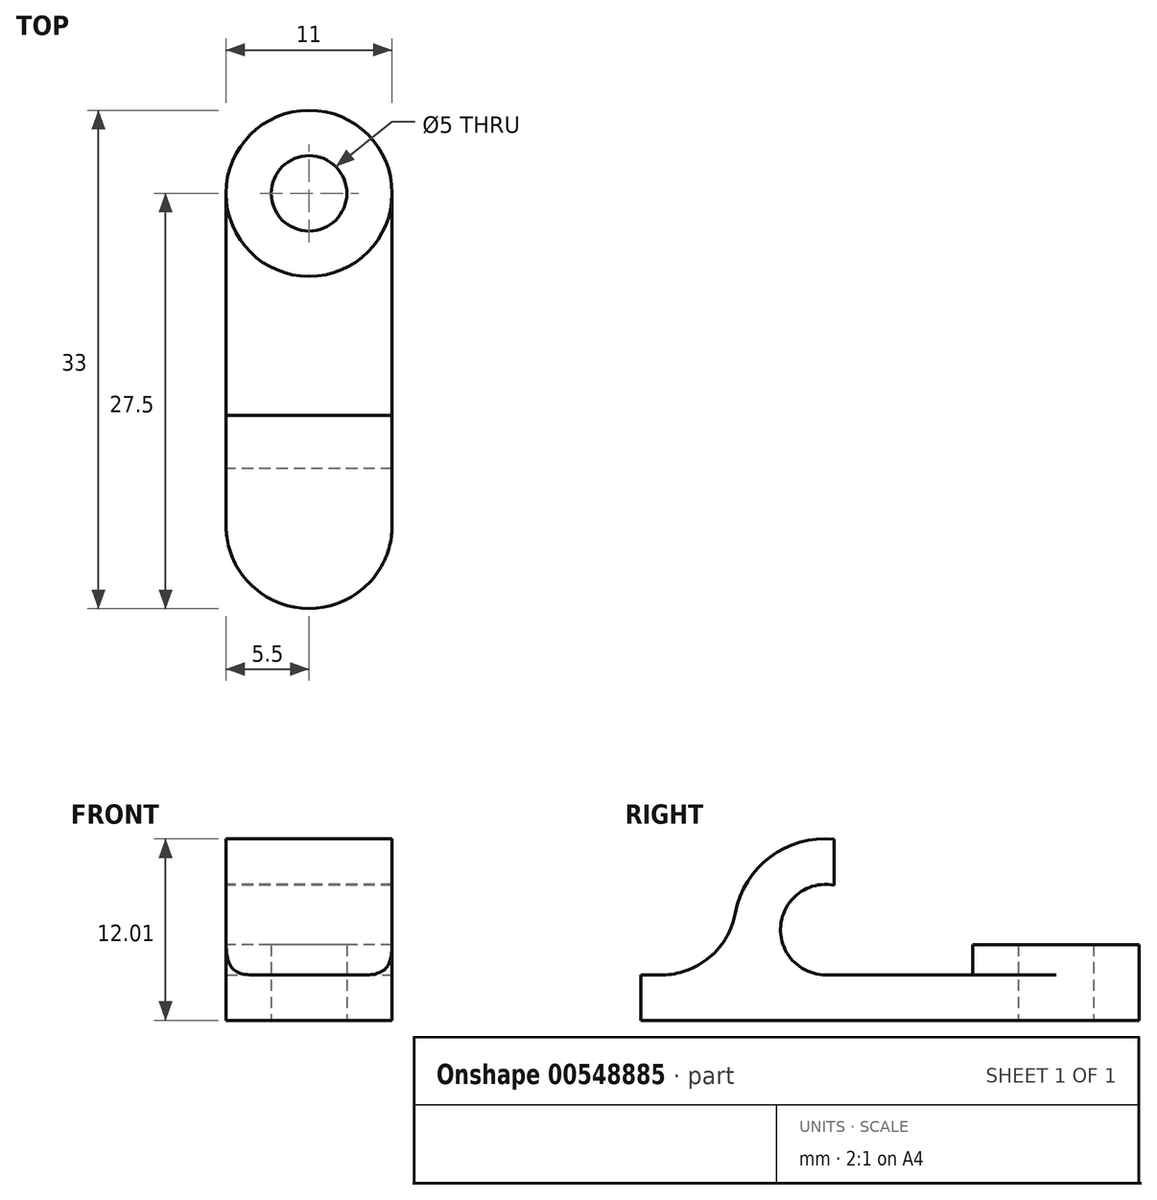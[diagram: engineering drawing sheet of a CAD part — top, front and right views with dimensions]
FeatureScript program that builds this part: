
annotation { "Feature Type Name" : "Feature", "Feature Type Description" : "" }
export const myFeature = defineFeature(function(context is Context, id is Id, definition is map)
    precondition{}
    {
        {
            var Q0;
            Q0=qCreatedBy(makeId("Top.planeOp"),FACE);
            var sketch = newSketch(context, id + "F0", { "sketchPlane" : qUnion([Q0])});
            skLineSegment(sketch, "E0.bottom", {"start": v(-5.5, -11) * mm, "end": v(5.5, -11) * mm});
            skLineSegment(sketch, "E0.top", {"start": v(-5.5, 11) * mm, "end": v(5.5, 11) * mm});
            skLineSegment(sketch, "E0.left", {"start": v(-5.5, -11) * mm, "end": v(-5.5, 11) * mm});
            skLineSegment(sketch, "E0.right", {"start": v(5.5, -11) * mm, "end": v(5.5, 11) * mm});
            skPoint(sketch, "E0.middle", {"position": v(0, 0) * mm});
            skCircle(sketch, "E1", {"center": v(0, 11) * mm, "radius": 5.5 * mm});
            skCircle(sketch, "E2", {"center": v(0, -11) * mm, "radius": 5.5 * mm});
            skCircle(sketch, "E3", {"center": v(0, 11) * mm, "radius": 2.5 * mm});
            skSolve(sketch);
        }
        {
            var Q0;
            {var subQ0=sQuery(id+"F0.wireOp",EDGE,"E0.left");Q0=makeQuery(id+"F0.imprint","IMPRINT",FACE,{"disambiguationData":[TD([[makeQuery(id+"F0.imprint","IMPRINT",EDGE,{"derivedFrom":subQ0}),-1.0]])]});}
            var Q1;
            {var subQ0=sQuery(id+"F0.wireOp",EDGE,"E0.bottom");Q1=makeQuery(id+"F0.imprint","IMPRINT",FACE,{"disambiguationData":[TD([[makeQuery(id+"F0.imprint","IMPRINT",EDGE,{"derivedFrom":subQ0}),1.0]])]});}
            var Q2;
            {var subQ0=sQuery(id+"F0.wireOp",EDGE,"E0.bottom");Q2=makeQuery(id+"F0.imprint","IMPRINT",FACE,{"disambiguationData":[TD([[makeQuery(id+"F0.imprint","IMPRINT",EDGE,{"derivedFrom":subQ0}),-1.0]])]});}
            extrude(context, id + "F1", {"entities" : qUnion([Q0, Q1, Q2]), "depth" : 3 * mm, "offsetDistance" : 25 * mm});
        }
        {
            var Q0;
            {var subQ1=sQuery(id+"F0.wireOp",EDGE,"E0.top");var subQ3=sQuery(id+"F0.wireOp",EDGE,"E3");var subQ4=makeQuery(id+"F0.imprint","INTERSECT",VERTEX,{"disambiguationData":[OD(0.0)],"derivedFrom":[subQ1,subQ3]});Q0=makeQuery(id+"F0.imprint","IMPRINT",FACE,{"disambiguationData":[TD([[makeQuery(id+"F0.imprint","IMPRINT",EDGE,{"disambiguationData":[TD([[subQ4,-1.0]])],"derivedFrom":subQ3}),-1.0]])]});}
            var Q1;
            {var subQ1=sQuery(id+"F0.wireOp",EDGE,"E0.top");var subQ3=sQuery(id+"F0.wireOp",EDGE,"E3");var subQ4=makeQuery(id+"F0.imprint","INTERSECT",VERTEX,{"disambiguationData":[OD(0.0)],"derivedFrom":[subQ1,subQ3]});Q1=makeQuery(id+"F0.imprint","IMPRINT",FACE,{"disambiguationData":[TD([[makeQuery(id+"F0.imprint","IMPRINT",EDGE,{"disambiguationData":[TD([[subQ4,1.0]])],"derivedFrom":subQ3}),-1.0]])]});}
            extrude(context, id + "F2", {"entities" : qUnion([Q0, Q1]), "operationType" : NewBodyOperationType.ADD, "depth" : 5 * mm, "offsetDistance" : 25 * mm});
        }
        {
            var Q0;
            Q0=makeQuery(id+"F1.opExtrude","SWEPT_FACE",FACE,{"disambiguationData":[OSD([sQuery(id+"F0.wireOp",EDGE,"E0.left")])]});
            var sketch = newSketch(context, id + "F3", { "sketchPlane" : qUnion([Q0])});
            skCircle(sketch, "E4", {"center": v(4.24, 6) * mm, "radius": 3 * mm});
            skArc(sketch, "E5", {"start": v(4.97, 0.04) * mm, "mid": v(10.3, 6.65) * mm, "end": v(3.7, 11.98) * mm});
            skLineSegment(sketch, "E6", {"start": v(3.7, 11.98) * mm, "end": v(3.7, 8.95) * mm});
            skSolve(sketch);
        }
        {
            var Q0;
            {var subQ0=sQuery(id+"F3.wireOp",EDGE,"E6");Q0=makeQuery(id+"F3.imprint","IMPRINT",FACE,{"disambiguationData":[TD([[makeQuery(id+"F3.imprint","IMPRINT",EDGE,{"derivedFrom":subQ0}),1.0]])]});}
            extrude(context, id + "F4", {"entities" : qUnion([Q0]), "operationType" : NewBodyOperationType.ADD, "oppositeDirection" : true, "depth" : 11 * mm, "offsetDistance" : 25 * mm});
        }
        {
            var Q0;
            Q0=makeQuery(id+"F4.opExtrude","SWEPT_EDGE",EDGE,{"disambiguationData":[OSD([sQuery(id+"F0.wireOp",EDGE,"E0.left"),sQuery(id+"F3.wireOp",EDGE,"E5")])]});
            fillet(context, id + "F5", {"entities" : qUnion([Q0]), "radius" : 5 * mm, "tangentPropagation" : true, "allowEdgeOverflow" : false});
        }
    });
